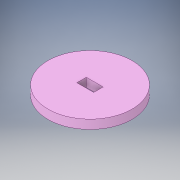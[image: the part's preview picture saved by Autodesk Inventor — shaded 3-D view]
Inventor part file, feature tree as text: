
AUTODESK INVENTOR PART (.ipt)
format: ipt  version: 2019 (Build 230136000, 136)  size: 112,128 bytes
history: native  units: mm
features: other x1, extrude x1, sketch x1
ambient origin geometry x8: Origin, YZ Plane, XZ Plane, XY Plane, X Axis, Y Axis, Z Axis, Center Point
bodies: Body1 (feature_tree)
feature tree (3):
  other  "Sólido1"
  extrude  "Extrusión1"  Depth=3.38mm
  sketch  "Boceto1"  dims[d0=6.0mm d1=3.38mm d2=30.0mm d3=3.18mm d4=0.0mm]
